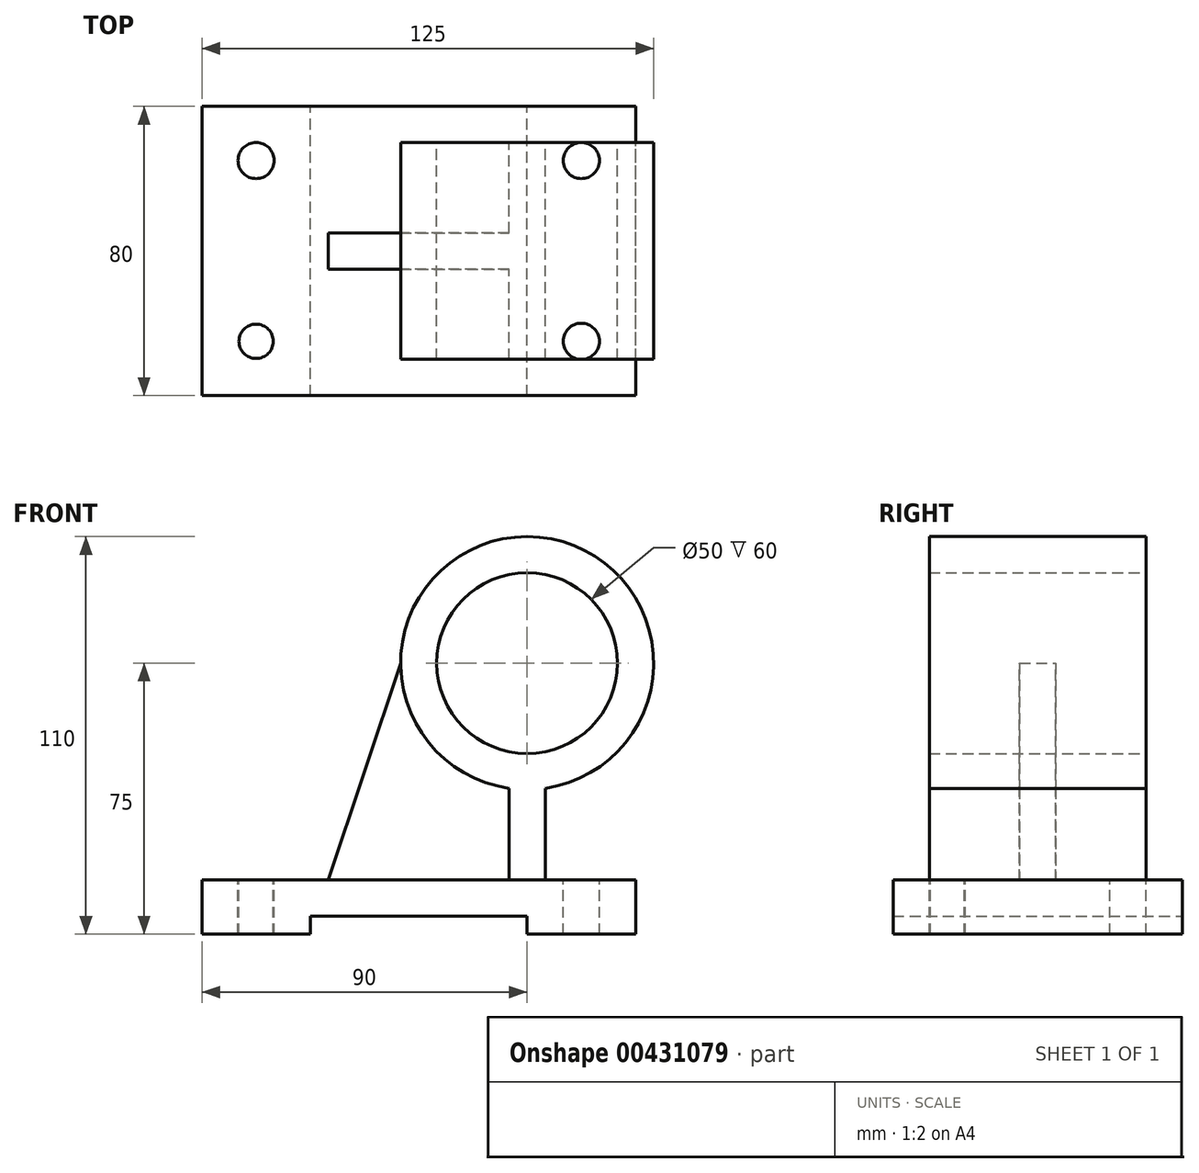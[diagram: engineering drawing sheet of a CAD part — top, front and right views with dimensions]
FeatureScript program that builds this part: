
annotation { "Feature Type Name" : "Feature", "Feature Type Description" : "" }
export const myFeature = defineFeature(function(context is Context, id is Id, definition is map)
    precondition{}
    {
        {
            var Q0;
            Q0=qCreatedBy(makeId("Front.planeOp"),FACE);
            var sketch = newSketch(context, id + "F0", { "sketchPlane" : qUnion([Q0])});
            skLineSegment(sketch, "E0.bottom", {"start": v(60, 7.5) * mm, "end": v(-60, 7.5) * mm});
            skLineSegment(sketch, "E0.top", {"start": v(60, -7.5) * mm, "end": v(30, -7.5) * mm});
            skLineSegment(sketch, "E0.left", {"start": v(60, 7.5) * mm, "end": v(60, -7.5) * mm});
            skLineSegment(sketch, "E0.right", {"start": v(-60, 7.5) * mm, "end": v(-60, -7.5) * mm});
            skPoint(sketch, "E0.middle", {"position": v(0, 0) * mm});
            skCircle(sketch, "E1", {"center": v(30, 67.5) * mm, "radius": 25 * mm});
            skCircle(sketch, "E2", {"center": v(30, 67.5) * mm, "radius": 35 * mm});
            skLineSegment(sketch, "E3", {"start": v(-60, -7.5) * mm, "end": v(-30, -7.5) * mm});
            skLineSegment(sketch, "E4", {"start": v(-30, -7.5) * mm, "end": v(-30, -2.5) * mm});
            skLineSegment(sketch, "E5", {"start": v(-30, -2.5) * mm, "end": v(30, -2.5) * mm});
            skLineSegment(sketch, "E6", {"start": v(30, -2.5) * mm, "end": v(30, -7.5) * mm});
            skLineSegment(sketch, "E7.trimOffspring", {"start": v(-30, -7.5) * mm, "end": v(-60, -7.5) * mm});
            skLineSegment(sketch, "E8", {"start": v(25, 32.86) * mm, "end": v(25, 7.5) * mm});
            skLineSegment(sketch, "E9", {"start": v(25, 7.5) * mm, "end": v(35, 7.5) * mm});
            skLineSegment(sketch, "E10", {"start": v(35, 7.5) * mm, "end": v(35, 32.86) * mm});
            skPoint(sketch, "E11.start.orphan", {"position": v(35, 67.5) * mm});
            skLineSegment(sketch, "E12", {"start": v(-60, 7.5) * mm, "end": v(-25, 7.5) * mm});
            skLineSegment(sketch, "E13", {"start": v(-25, 7.5) * mm, "end": v(-5, 67.46) * mm});
            skSolve(sketch);
        }
        {
            var Q0;
            {var subQ0=sQuery(id+"F0.wireOp",EDGE,"E0.left");Q0=makeQuery(id+"F0.imprint","IMPRINT",FACE,{"disambiguationData":[TD([[makeQuery(id+"F0.imprint","IMPRINT",EDGE,{"derivedFrom":subQ0}),-1.0]])]});}
            extrude(context, id + "F1", {"entities" : qUnion([Q0]), "depth" : 40 * mm, "hasSecondDirection" : true, "secondDirectionOppositeDirection" : true, "secondDirectionDepth" : 40 * mm});
        }
        {
            var Q0;
            {var subQ2=sQuery(id+"F0.wireOp",EDGE,"E8");Q0=makeQuery(id+"F0.imprint","IMPRINT",FACE,{"disambiguationData":[TD([[makeQuery(id+"F0.imprint","IMPRINT",EDGE,{"derivedFrom":subQ2}),-1.0]])]});}
            extrude(context, id + "F2", {"entities" : qUnion([Q0]), "depth" : 5 * mm, "hasSecondDirection" : true, "secondDirectionOppositeDirection" : true, "secondDirectionDepth" : 5 * mm});
        }
        {
            var Q0;
            Q0=makeQuery(id+"F0.imprint","IMPRINT",FACE,{"disambiguationData":[TD([[makeQuery(id+"F0.imprint","IMPRINT",EDGE,{"derivedFrom":sQuery(id+"F0.wireOp",EDGE,"E1")}),-1.0]])]});
            var Q1;
            {var subQ0=sQuery(id+"F0.wireOp",EDGE,"E8");Q1=makeQuery(id+"F0.imprint","IMPRINT",FACE,{"disambiguationData":[TD([[makeQuery(id+"F0.imprint","IMPRINT",EDGE,{"derivedFrom":subQ0}),1.0]])]});}
            extrude(context, id + "F3", {"entities" : qUnion([Q0, Q1]), "operationType" : NewBodyOperationType.ADD, "depth" : 30 * mm, "hasSecondDirection" : true, "secondDirectionOppositeDirection" : true, "secondDirectionDepth" : 30 * mm});
        }
        {
            var Q0;
            Q0=makeQuery(id+"F1.opExtrude","SWEPT_FACE",FACE,{"disambiguationData":[OSD([sQuery(id+"F0.wireOp",EDGE,"E0.bottom"),sQuery(id+"F0.wireOp",EDGE,"E9"),sQuery(id+"F0.wireOp",EDGE,"E12")])]});
            var sketch = newSketch(context, id + "F4", { "sketchPlane" : qUnion([Q0])});
            skLineSegment(sketch, "E14", {"start": v(-60, 40) * mm, "end": v(-25, 40) * mm});
            skLineSegment(sketch, "E15", {"start": v(-25, 40) * mm, "end": v(-25, -40) * mm});
            skLineSegment(sketch, "E16", {"start": v(-25, -40) * mm, "end": v(-60, -40) * mm});
            skLineSegment(sketch, "E17", {"start": v(-60, -40) * mm, "end": v(-60, 40) * mm});
            skLineSegment(sketch, "E18", {"start": v(-60, 0) * mm, "end": v(-60, 25) * mm});
            skLineSegment(sketch, "E19", {"start": v(-60, 25) * mm, "end": v(-60, 0) * mm});
            skLineSegment(sketch, "E20", {"start": v(-60, 0) * mm, "end": v(-60, -25) * mm});
            skLineSegment(sketch, "E21", {"start": v(-60, -40) * mm, "end": v(-45, -40) * mm});
            skCircle(sketch, "E22", {"center": v(-45, -25) * mm, "radius": 4.75 * mm});
            skLineSegment(sketch, "E23", {"start": v(-60, 40) * mm, "end": v(-45, 40) * mm});
            skCircle(sketch, "E24", {"center": v(-45, 25) * mm, "radius": 5 * mm});
            skSolve(sketch);
        }
        {
            var Q0;
            Q0=makeQuery(id+"F4.imprint","IMPRINT",FACE,{"disambiguationData":[TD([[makeQuery(id+"F4.imprint","IMPRINT",EDGE,{"derivedFrom":sQuery(id+"F4.wireOp",EDGE,"E24")}),1.0]])]});
            var Q1;
            Q1=makeQuery(id+"F4.imprint","IMPRINT",FACE,{"disambiguationData":[TD([[makeQuery(id+"F4.imprint","IMPRINT",EDGE,{"derivedFrom":sQuery(id+"F4.wireOp",EDGE,"E22")}),1.0]])]});
            extrude(context, id + "F5", {"entities" : qUnion([Q0, Q1]), "operationType" : NewBodyOperationType.REMOVE, "oppositeDirection" : true, "depth" : 25 * mm});
        }
        {
            var Q0;
            Q0=makeQuery(id+"F1.opExtrude","SWEPT_FACE",FACE,{"disambiguationData":[OSD([sQuery(id+"F0.wireOp",EDGE,"E0.bottom"),sQuery(id+"F0.wireOp",EDGE,"E9"),sQuery(id+"F0.wireOp",EDGE,"E12")])]});
            var sketch = newSketch(context, id + "F6", { "sketchPlane" : qUnion([Q0])});
            skLineSegment(sketch, "E25", {"start": v(60, -40) * mm, "end": v(45, -40) * mm});
            skLineSegment(sketch, "E26", {"start": v(60, -40) * mm, "end": v(60, -25) * mm});
            skCircle(sketch, "E27", {"center": v(45, -25) * mm, "radius": 5 * mm});
            skLineSegment(sketch, "E28", {"start": v(60, 40) * mm, "end": v(60, 25) * mm});
            skLineSegment(sketch, "E29", {"start": v(60, 25) * mm, "end": v(60, 40) * mm});
            skLineSegment(sketch, "E30", {"start": v(60, 40) * mm, "end": v(45, 40) * mm});
            skCircle(sketch, "E31", {"center": v(45, 25) * mm, "radius": 5 * mm});
            skSolve(sketch);
        }
        {
            var Q0;
            Q0 = qSketchRegion(id + "F6", true);
            extrude(context, id + "F7", {"entities" : qUnion([Q0]), "operationType" : NewBodyOperationType.REMOVE, "oppositeDirection" : true, "depth" : 25 * mm});
        }
    });
